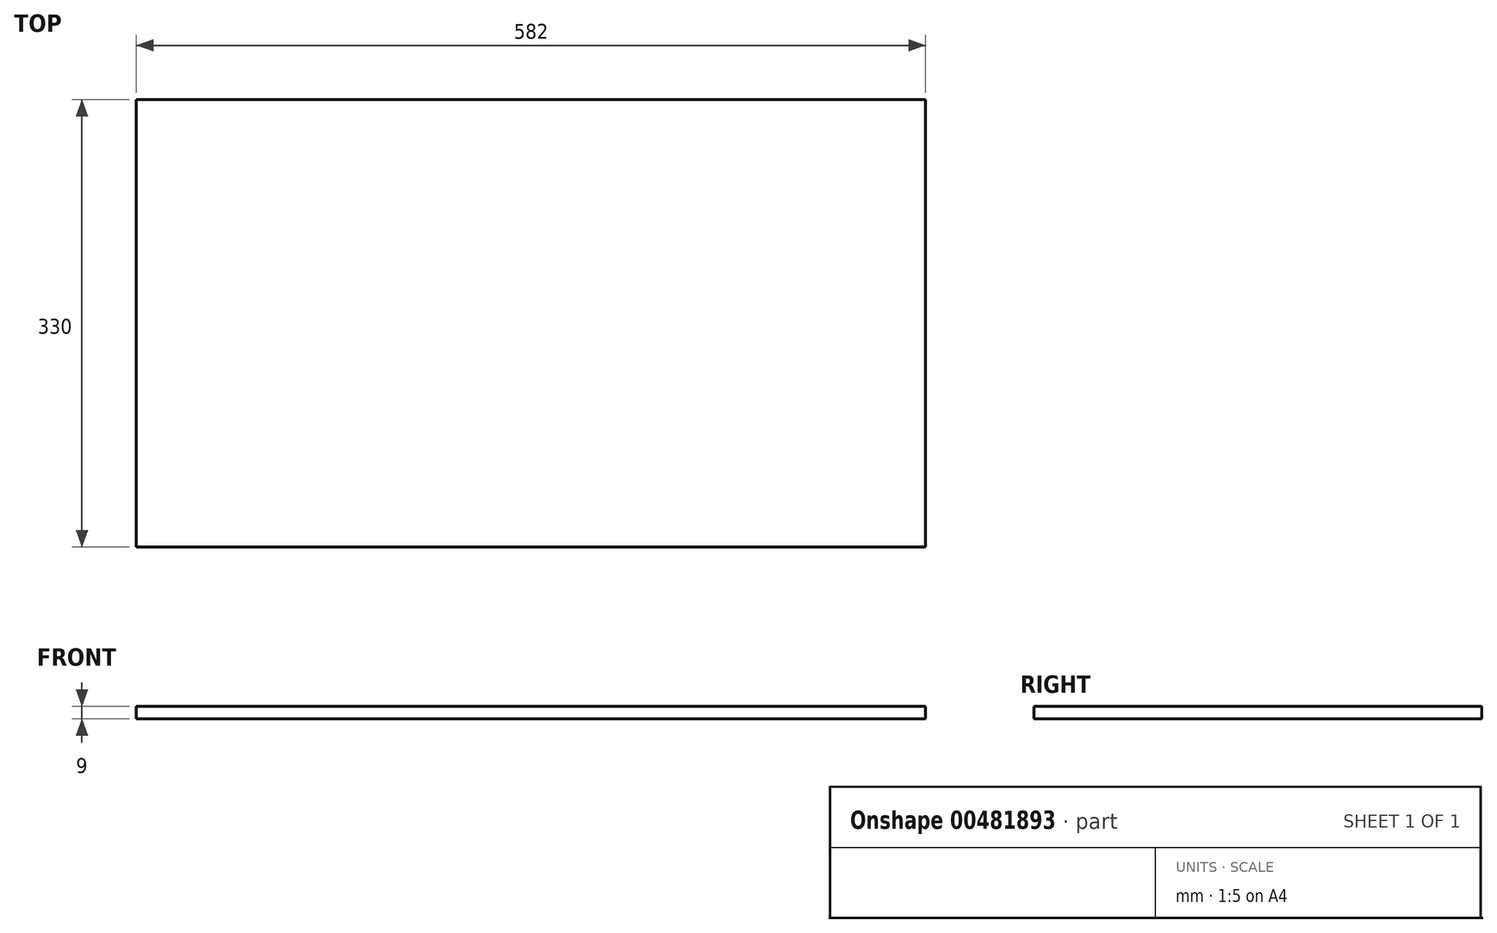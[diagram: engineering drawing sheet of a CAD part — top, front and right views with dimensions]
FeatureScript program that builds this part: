
annotation { "Feature Type Name" : "Feature", "Feature Type Description" : "" }
export const myFeature = defineFeature(function(context is Context, id is Id, definition is map)
    precondition{}
    {
        {
            var Q0;
            Q0=qCreatedBy(makeId("Top.planeOp"),FACE);
            var sketch = newSketch(context, id + "F0", { "sketchPlane" : qUnion([Q0])});
            skLineSegment(sketch, "E0.bottom", {"start": v(0, 0) * mm, "end": v(582, 0) * mm});
            skLineSegment(sketch, "E0.top", {"start": v(0, 330) * mm, "end": v(582, 330) * mm});
            skLineSegment(sketch, "E0.left", {"start": v(0, 0) * mm, "end": v(0, 330) * mm});
            skLineSegment(sketch, "E0.right", {"start": v(582, 0) * mm, "end": v(582, 330) * mm});
            skSolve(sketch);
        }
        {
            var Q0;
            Q0 = qSketchRegion(id + "F0", true);
            extrude(context, id + "F1", {"entities" : qUnion([Q0]), "depth" : 9 * mm});
        }
    });
